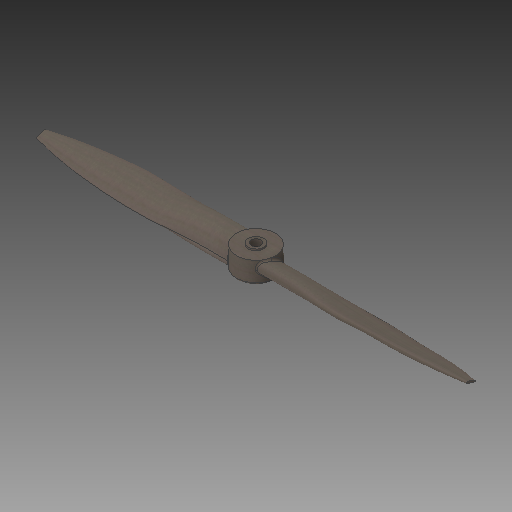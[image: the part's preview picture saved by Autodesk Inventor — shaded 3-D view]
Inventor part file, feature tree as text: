
AUTODESK INVENTOR PART (.ipt)
format: ipt  version: 2018 (Build 220112000, 112)  size: 1,660,928 bytes
history: native  units: mm
features: sketch x9, plane x7, other x3, revolve x1, loft x1, fillet x1, pattern_circular x1
ambient origin geometry x8: Origin, YZ Plane, XZ Plane, XY Plane, X Axis, Y Axis, Z Axis, Center Point
bodies: Solid1 (feature_tree)
feature tree (23):
  revolve  "Revolution1"  [1 undecoded]
  plane  "Work Plane1"
  plane  "Work Plane2"
  plane  "Work Plane3"
  plane  "Work Plane4"
  plane  "Work Plane5"
  plane  "Work Plane6"
  sketch  "Sketch2"  dims[d2=3.0mm d3=1.5mm d4=22.0mm]
  sketch  "Sketch3"  dims[d5=2.0mm]
  sketch  "Sketch4"  dims[d6=1.5mm]
  sketch  "Sketch5"  dims[d7=1.5mm]
  sketch  "Sketch6"  dims[d8=90.0deg]
  sketch  "Sketch7"  dims[d9=56.14mm d10=96.77mm d11=126.14mm d12=157.8mm d13=189.33mm d14=220.0mm d20=40.0mm]
  plane  "Work Plane7"
  sketch  "Sketch8"  dims[d24=33.278655mm]
  loft  "Loft1"
  fillet  "Fillet1"  Radius=22.0mm
  other  "Work Axis1"
  pattern_circular  "Circular Pattern1"  Count=4  [1 undecoded]
  sketch  "Sketch1"  dims[d0=5.0mm d1=20.0mm]
  other  "Image1"
  sketch  "Sketch10"  dims[d76=8.695358mm d84=13.02mm d85=15.153mm d86=15.153mm d87=13.012mm d88=9.821mm d95=13.02mm d96=15.153mm d97=15.153mm d98=13.012mm d99=9.821mm d100=221.460376mm d102=176.089529mm d131=13.02mm d132=10.0mm d135=15.153mm d136=10.0mm d142=10.0mm d143=15.153mm d150=13.012mm d151=10.0mm d152=9.821mm d153=10.0mm d154=12.0mm d155=0.0mm d156=90.0deg d157=0.0mm d158=90.0deg d159=0.0mm d160=90.0deg d161=0.0mm d162=90.0deg d163=0.0mm d164=90.0deg d165=0.0mm d166=90.0deg d167=0.0mm d168=90.0deg d169=2.0mm d170=2.0mm d171=2.0mm d172=7.436mm d173=2.0mm d174=7.969mm d175=2.0mm d176=5.859mm d177=2.0mm d178=0.313mm d179=2.0mm d180=8.125mm d181=2.0mm d182=9.277mm d183=2.0mm d184=1.18mm d185=20.0mm d186=360.0deg]
  other  "Work Axis2"
note: 2 required parameter values undecoded (feature->parameter linkage not recoverable at this tier; creation-order binding heuristic only, values carry confidence <= 0.55)